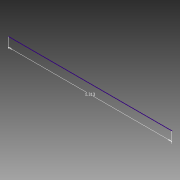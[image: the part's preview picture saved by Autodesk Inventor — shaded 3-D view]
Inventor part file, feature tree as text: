
AUTODESK INVENTOR PART (.ipt)
format: ipt  version: 2013 (Build 170138000, 138)  size: 57,344 bytes
history: native  units: in
note: dims shown in document units (in); Inventor stores cm internally (conversion verified against a paired STEP export)
features: sketch x1
ambient origin geometry x8: Origin, YZ Plane, XZ Plane, XY Plane, X Axis, Y Axis, Z Axis, Center Point
feature tree (1):
  sketch  "Sketch1"  dims[d0=1.3125in]
